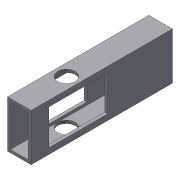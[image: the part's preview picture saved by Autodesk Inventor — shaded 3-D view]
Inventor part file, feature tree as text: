
AUTODESK INVENTOR PART (.ipt)
format: ipt  version: 2012 (Build 160160000, 160)  size: 75,264 bytes
history: native  units: in
note: dims shown in document units (in); Inventor stores cm internally (conversion verified against a paired STEP export)
features: extrude x1, shell x1, sketch x1
ambient origin geometry x8: Origin, YZ Plane, XZ Plane, XY Plane, X Axis, Y Axis, Z Axis, Center Point
bodies: Solid1 (feature_tree)
feature tree (3):
  extrude  "Extrusion1"  Depth=2.0in
  shell  "Shell1"  Thickness=6.0in
  sketch  "Sketch1"  dims[d0=1.0in d1=2.0in d2=6.0in d3=0.0in d4=0.125in]
